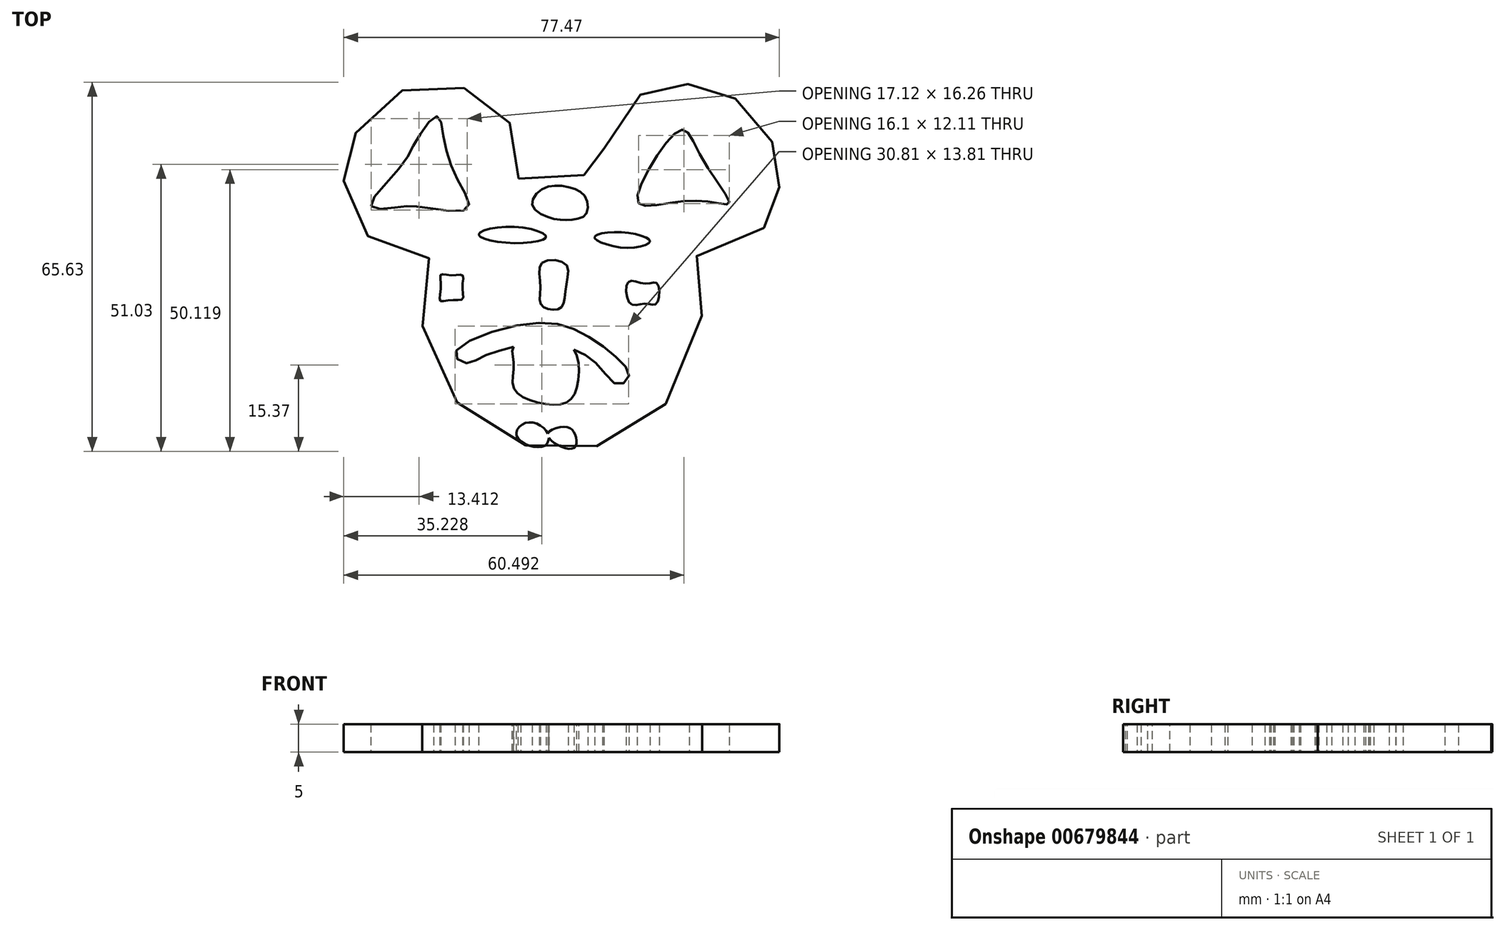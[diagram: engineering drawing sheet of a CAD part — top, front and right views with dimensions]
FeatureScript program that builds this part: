
annotation { "Feature Type Name" : "Feature", "Feature Type Description" : "" }
export const myFeature = defineFeature(function(context is Context, id is Id, definition is map)
    precondition{}
    {
        {
            var Q0;
            Q0=qCreatedBy(makeId("Top.planeOp"),FACE);
            var sketch = newSketch(context, id + "F0", { "sketchPlane" : qUnion([Q0])});
            skFitSpline(sketch, "E0", {"points": [v(-43.65, 53.33) * mm, v(-40.4, 54.02) * mm, v(-34.04, 54.4) * mm, v(-28.55, 53.33) * mm, v(-28.5, 53.83) * mm, v(-28.68, 56.83) * mm, v(-28, 60.76) * mm, v(-26.27, 64.82) * mm, v(-19.35, 69.6) * mm, v(-16.47, 70.26) * mm, v(-15.26, 70.26) * mm, v(-12.97, 70.1) * mm, v(-10.3, 69.72) * mm, v(-7.52, 68.79) * mm, v(-3.73, 66.58) * mm, v(-0.71, 63.4) * mm, v(1.2, 60.4) * mm, v(2.48, 56.9) * mm, v(2.72, 55.13) * mm, v(2.73, 52.12) * mm, v(2.66, 51.02) * mm, v(1.81, 47.92) * mm, v(0.95, 46.2) * mm, v(-1.2, 43.12) * mm, v(-8.1, 39.46) * mm, v(-13.2, 39.46) * mm, v(-12.1, 36.79) * mm, v(-11.43, 25.9) * mm, v(-16.2, 14.9) * mm, v(-21.2, 9.89) * mm, v(-29.5, 5.8) * mm, v(-39.41, 4.95) * mm, v(-41.6, 5.65) * mm, v(-47.59, 7.94) * mm, v(-54.87, 13.9) * mm, v(-59.5, 22.39) * mm, v(-60.66, 30.47) * mm, v(-58.74, 39.2) * mm, v(-59.23, 39.24) * mm, v(-64, 39.5) * mm, v(-68.88, 41.75) * mm, v(-73.44, 47) * mm, v(-74.63, 51) * mm, v(-74.71, 53.88) * mm, v(-74.34, 56.64) * mm, v(-73.4, 59.9) * mm, v(-71.52, 63.08) * mm, v(-67.7, 67.14) * mm, v(-63.27, 69.42) * mm, v(-58.04, 70.46) * mm, v(-53.42, 69.48) * mm, v(-50.22, 68.6) * mm, v(-46.49, 65.25) * mm, v(-43.93, 60.22) * mm, v(-43.34, 55.47) * mm, v(-43.65, 53.33) * mm]});
            skFitSpline(sketch, "E1", {"points": [v(-44.38, 44.78) * mm, v(-50.73, 43.42) * mm, v(-45.22, 41.9) * mm, v(-38.77, 42.95) * mm, v(-44.38, 44.78) * mm]});
            skFitSpline(sketch, "E2", {"points": [v(-25.37, 43.8) * mm, v(-30.12, 42.9) * mm, v(-24.58, 41.03) * mm, v(-20.27, 42.21) * mm, v(-25.37, 43.8) * mm]});
            skFitSpline(sketch, "E3", {"points": [v(-54.95, 22.25) * mm, v(-43.05, 27.4) * mm, v(-33, 26.21) * mm, v(-26, 21.32) * mm, v(-24.02, 18.15) * mm, v(-26, 16.7) * mm, v(-29.57, 20.26) * mm, v(-33.8, 22.9) * mm, v(-38.56, 24.36) * mm, v(-44.5, 23.44) * mm, v(-50.2, 21.59) * mm, v(-53.1, 20.53) * mm, v(-54.95, 22.25) * mm]});
            skFitSpline(sketch, "E4", {"points": [v(-39.48, 38.37) * mm, v(-39.75, 34.4) * mm, v(-39.75, 31.1) * mm, v(-37.9, 30.05) * mm, v(-35.91, 30.58) * mm, v(-35.25, 34.01) * mm, v(-35.25, 38.11) * mm, v(-39.48, 38.37) * mm]});
            skFitSpline(sketch, "E5", {"points": [v(-42.13, 9.95) * mm, v(-43.98, 7.58) * mm, v(-39.41, 5.65) * mm, v(-38.43, 7.97) * mm, v(-42.13, 9.95) * mm]});
            skPoint(sketch, "E6.2.internal.snap0", {"position": v(-36.06, 4.95) * mm});
            skFitSpline(sketch, "E6", {"points": [v(-35.25, 9.16) * mm, v(-38.43, 7.97) * mm, v(-36.06, 5.65) * mm, v(-33.53, 5.65) * mm, v(-33.67, 7.97) * mm, v(-35.25, 9.16) * mm]});
            skFitSpline(sketch, "E7", {"points": [v(-69.89, 48.42) * mm, v(-64.73, 48.29) * mm, v(-60.77, 48.29) * mm, v(-52.7, 48.02) * mm, v(-54.16, 52.52) * mm, v(-56.93, 60.32) * mm, v(-58.12, 64.42) * mm, v(-61.56, 60.58) * mm, v(-64.86, 55.16) * mm, v(-69.89, 48.42) * mm]});
            skFitSpline(sketch, "E8", {"points": [v(-22.3, 48.95) * mm, v(-16.48, 49.08) * mm, v(-8.68, 49.08) * mm, v(-6.17, 48.95) * mm, v(-10.93, 56.75) * mm, v(-14.37, 62.04) * mm, v(-19.52, 56.62) * mm, v(-22.3, 48.95) * mm]});
            skFitSpline(sketch, "E9", {"points": [v(-41.2, 48.68) * mm, v(-39.22, 51.6) * mm, v(-34.86, 51.86) * mm, v(-31.82, 50.14) * mm, v(-31.68, 46.97) * mm, v(-34.33, 46.04) * mm, v(-37.9, 46.3) * mm, v(-41.2, 48.68) * mm]});
            skFitSpline(sketch, "E10", {"points": [v(-55.61, 36.13) * mm, v(-53.63, 36.13) * mm, v(-53.63, 34.14) * mm, v(-53.63, 31.9) * mm, v(-55.74, 31.77) * mm, v(-57.6, 31.63) * mm, v(-57.46, 34.01) * mm, v(-57.46, 36.26) * mm, v(-55.61, 36.13) * mm]});
            skFitSpline(sketch, "E11", {"points": [v(-24.15, 34.94) * mm, v(-21.1, 34.67) * mm, v(-19, 34.67) * mm, v(-19.13, 31.1) * mm, v(-21.1, 31.1) * mm, v(-23.75, 31.1) * mm, v(-24.15, 34.94) * mm]});
            skFitSpline(sketch, "E12", {"points": [v(-44.5, 23.44) * mm, v(-44.5, 20.53) * mm, v(-44.5, 16.17) * mm, v(-40.7, 13.66) * mm, v(-35.15, 13.52) * mm, v(-33.1, 16.96) * mm, v(-33.8, 22.9) * mm, v(-38.56, 24.36) * mm, v(-44.5, 23.44) * mm]});
            skSolve(sketch);
        }
        {
            var Q0;
            Q0 = qSketchRegion(id + "F0", true);
            extrude(context, id + "F1", {"entities" : qUnion([Q0]), "depth" : 5 * mm, "offsetDistance" : 25.4 * mm});
        }
    });
